# Revit family: Showerhead-DXV-Slim_Square_D35700442_Series
name_source: partatom
category: Plumbing Fixtures
units: mm (PartAtom-declared; Revit-internal decimal feet)

## family parameters
Always vertical = No
Cut with Voids When Loaded = No
OmniClass Number = 23.45.05.14.17
OmniClass Title = Showers
Part Type = Normal
Room Calculation Point = No
Round Connector Dimension = Use Diameter
Shared = Yes
Work Plane-Based = Yes

## types (2) — shared parameters
Assembly Code = D2010710
CW Connection = No
CWFU = 3
Default Elevation = 0"
Description = Slim Square 12 Inch Showerhead Contemporary Accents Collection
Flow Rate = 2.5 gpm.  (9.5 L/min.)
HW Connection = No
HWFU = 3
Length = 11 13/16"
Manufacturer = DXV
Price = Prices may vary. Please consult Manufacturer Representative for most up-to-date price list.
Product Documentation Link = https://dxv01.blob.core.windows.net
Product Page URL = https://www.dxv.com
Revised Date = 02/11/2022
Tempered Water Connection = Yes
URL = https://www.dxv.com
Vent Connection = No
WFU = 4
Warranty Documentation Link = https://www.dxv.com
Waste Connection = No
Water Connection Diameter = 1/2"
Width = 11 13/16"

## per-type parameters (varying)
| type | Finish | Material | Model |
| D35700442.100 | Brass-DXV-100-Polished Chrome | Brass-DXV-100-Polished Chrome | D35700442.100 |
| D35701422.144 | Brass-DXV-144-Brushed Nickel | Brass-DXV-144-Brushed Nickel | D35700442.144 |

## geometry (parser evidence)
native form markers: Sweep x3
no freeform markers — native parametric forms only
